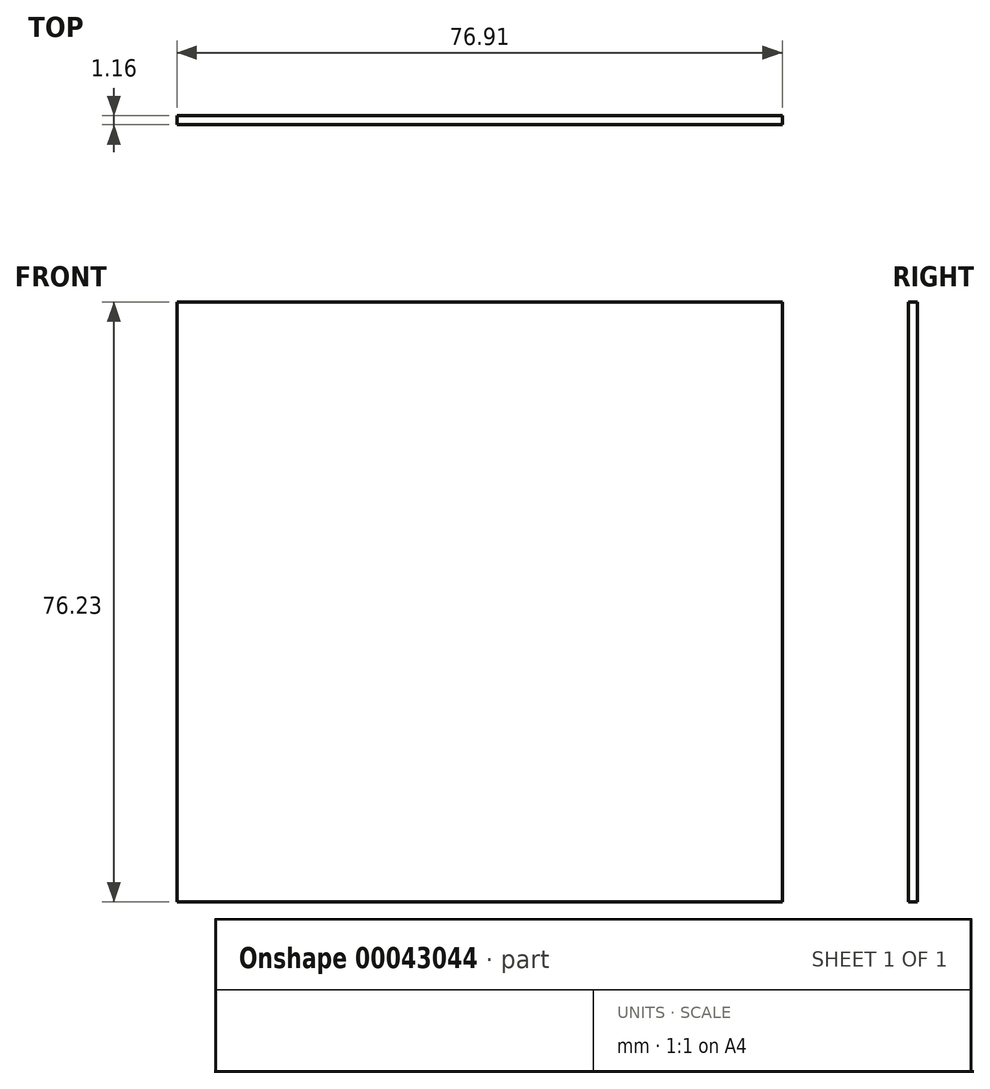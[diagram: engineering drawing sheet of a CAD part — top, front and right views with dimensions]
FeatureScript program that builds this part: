
annotation { "Feature Type Name" : "Feature", "Feature Type Description" : "" }
export const myFeature = defineFeature(function(context is Context, id is Id, definition is map)
    precondition{}
    {
        {
            var Q0;
            Q0=qCreatedBy(makeId("Front.planeOp"),FACE);
            var sketch = newSketch(context, id + "F0", { "sketchPlane" : qUnion([Q0])});
            skLineSegment(sketch, "E0.bottom", {"start": v(-76.9, 76.23) * mm, "end": v(0, 76.23) * mm});
            skLineSegment(sketch, "E0.top", {"start": v(-76.9, 0) * mm, "end": v(0, 0) * mm});
            skLineSegment(sketch, "E0.left", {"start": v(-76.9, 76.23) * mm, "end": v(-76.9, 0) * mm});
            skLineSegment(sketch, "E0.right", {"start": v(0, 76.23) * mm, "end": v(0, 0) * mm});
            skLineSegment(sketch, "E1.0", {"start": v(-6.35, 76.23) * mm, "end": v(-6.35, 0) * mm});
            skSolve(sketch);
        }
        {
            var Q0;
            Q0 = qSketchRegion(id + "F0", true);
            extrude(context, id + "F1", {"entities" : qUnion([Q0]), "depth" : 1.16 * mm});
        }
    });
